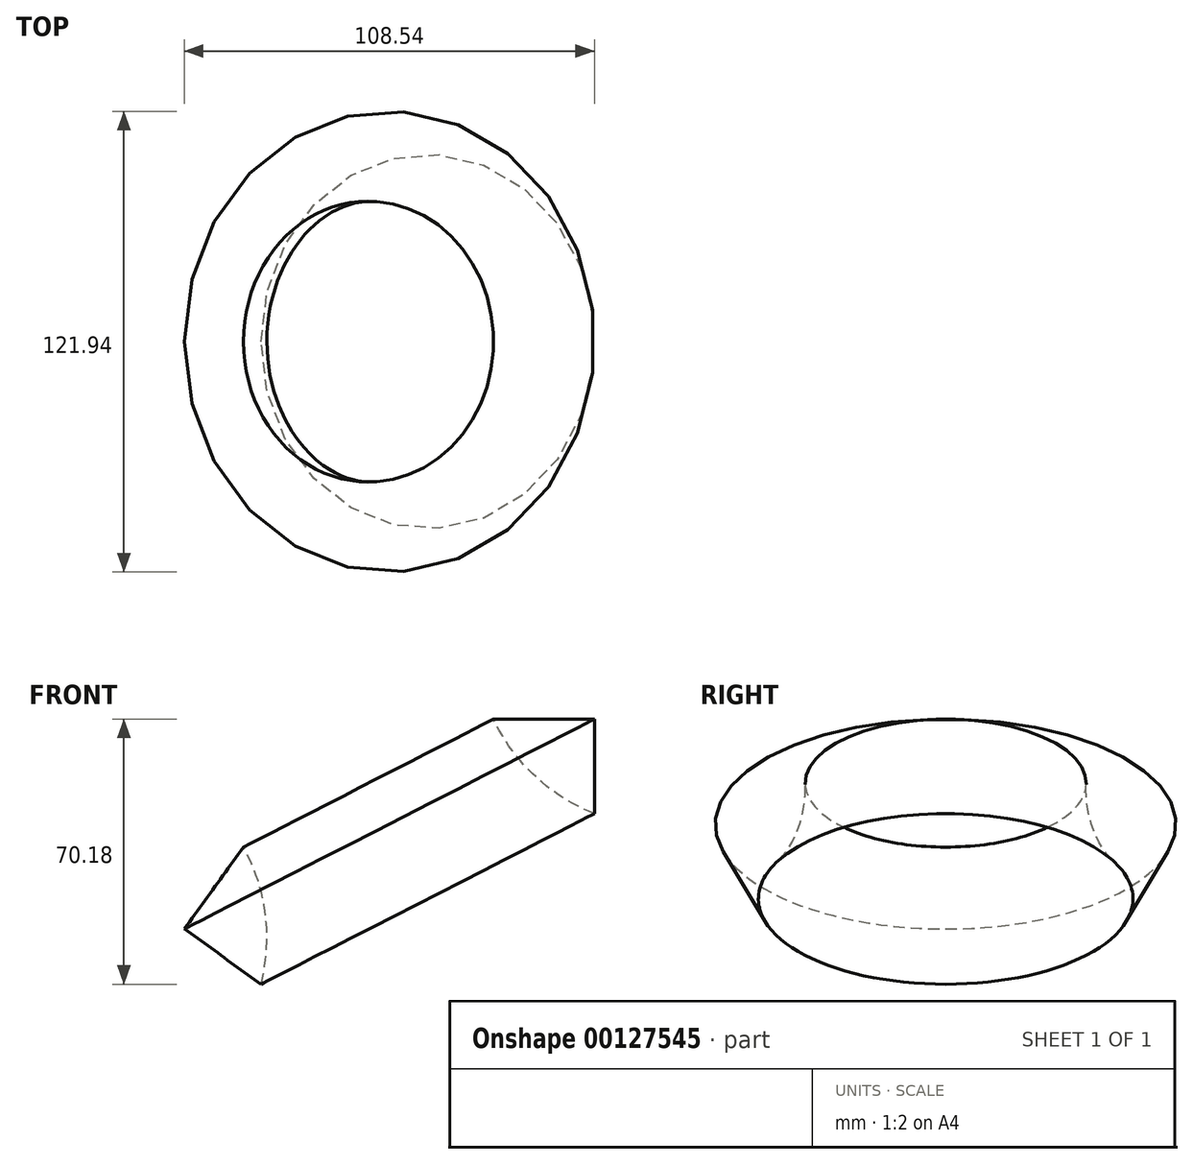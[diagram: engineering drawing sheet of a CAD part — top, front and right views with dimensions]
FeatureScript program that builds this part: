
annotation { "Feature Type Name" : "Feature", "Feature Type Description" : "" }
export const myFeature = defineFeature(function(context is Context, id is Id, definition is map)
    precondition{}
    {
        {
            var Q0;
            Q0=qCreatedBy(makeId("Front.planeOp"),FACE);
            var sketch = newSketch(context, id + "F0", { "sketchPlane" : qUnion([Q0])});
            skLineSegment(sketch, "E0.bottom", {"start": v(0, 0) * mm, "end": v(45.11, 0) * mm});
            skLineSegment(sketch, "E0.top", {"start": v(0, 45.67) * mm, "end": v(45.11, 45.67) * mm});
            skLineSegment(sketch, "E0.left", {"start": v(0, 0) * mm, "end": v(0, 45.67) * mm});
            skLineSegment(sketch, "E0.right", {"start": v(45.11, 0) * mm, "end": v(45.11, 45.67) * mm});
            skCircle(sketch, "E1", {"center": v(63.2, 66.75) * mm, "radius": 49.5 * mm});
            skLineSegment(sketch, "E2", {"start": v(0, 0) * mm, "end": v(-32.84, 64.17) * mm});
            skSolve(sketch);
        }
        {
            var Q0;
            {var subQ0=sQuery(id+"F0.wireOp",EDGE,"E0.right");var subQ1=sQuery(id+"F0.wireOp",EDGE,"E0.top");var subQ2=makeQuery(id+"F0.imprint","INTERSECT",VERTEX,{"derivedFrom":[subQ1,subQ0]});Q0=makeQuery(id+"F0.imprint","IMPRINT",FACE,{"disambiguationData":[TD([[makeQuery(id+"F0.imprint","IMPRINT",EDGE,{"disambiguationData":[TD([[subQ2,1.0]])],"derivedFrom":subQ1}),-1.0]])]});}
            var Q1;
            Q1=sQuery(id+"F0.wireOp",EDGE,"E2");
            revolve(context, id + "F1", {"entities" : qUnion([Q0]), "axis" : qUnion([Q1]), "revolveType" : RevolveType.FULL});
        }
    });
